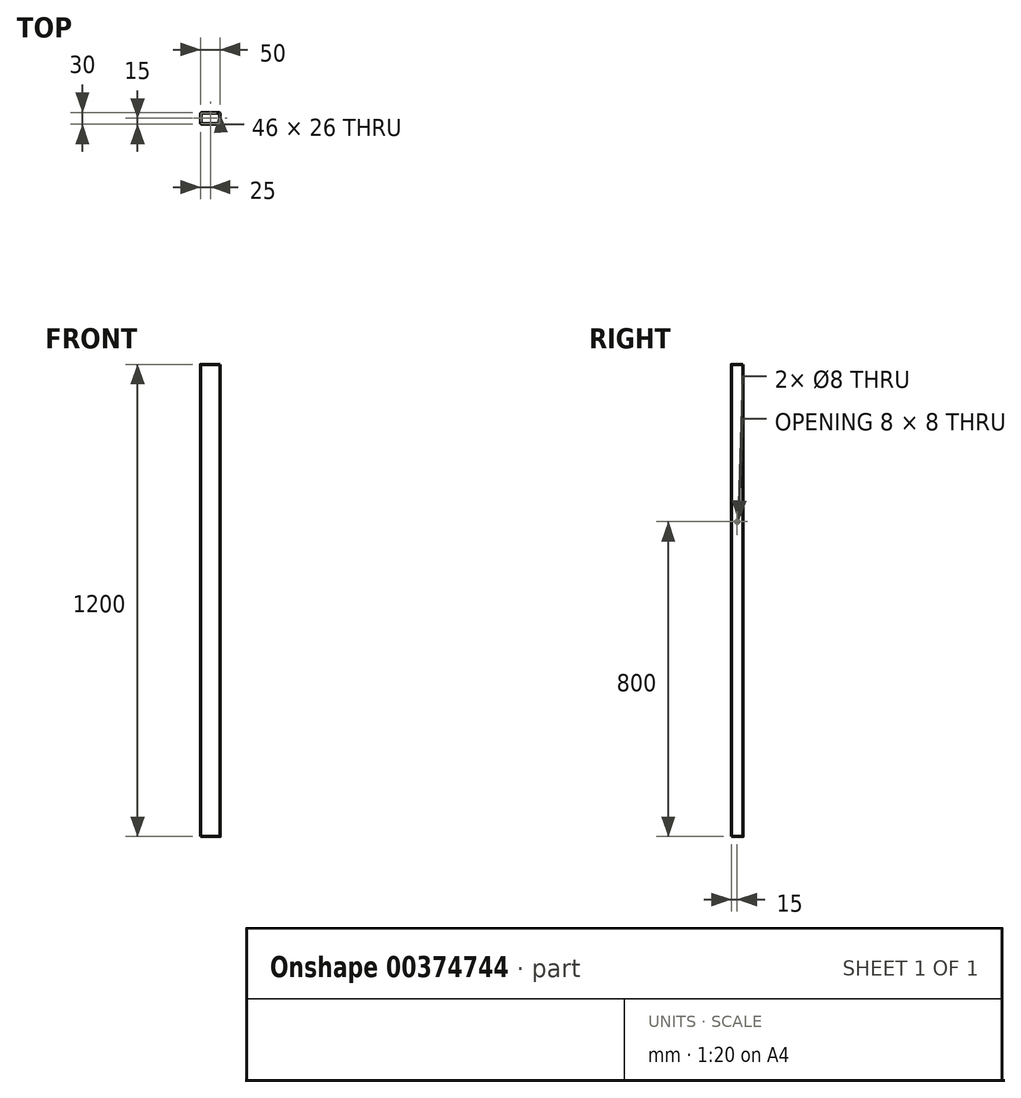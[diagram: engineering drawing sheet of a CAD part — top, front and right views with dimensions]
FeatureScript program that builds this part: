
annotation { "Feature Type Name" : "Feature", "Feature Type Description" : "" }
export const myFeature = defineFeature(function(context is Context, id is Id, definition is map)
    precondition{}
    {
        {
            var Q0;
            Q0=qCreatedBy(makeId("Top.planeOp"),FACE);
            var sketch = newSketch(context, id + "F0", { "sketchPlane" : qUnion([Q0])});
            skLineSegment(sketch, "E0.bottom", {"start": v(21.5, 15) * mm, "end": v(-21.5, 15) * mm});
            skLineSegment(sketch, "E0.top", {"start": v(21.5, -15) * mm, "end": v(-21.5, -15) * mm});
            skLineSegment(sketch, "E0.left", {"start": v(25, 11.5) * mm, "end": v(25, -11.5) * mm});
            skLineSegment(sketch, "E0.right", {"start": v(-25, 11.5) * mm, "end": v(-25, -11.5) * mm});
            skPoint(sketch, "E0.middle", {"position": v(0, 0) * mm});
            skLineSegment(sketch, "E1.bottom", {"start": v(23, -13) * mm, "end": v(-23, -13) * mm});
            skLineSegment(sketch, "E1.top", {"start": v(23, 13) * mm, "end": v(-23, 13) * mm});
            skLineSegment(sketch, "E1.left", {"start": v(23, -13) * mm, "end": v(23, 13) * mm});
            skLineSegment(sketch, "E1.right", {"start": v(-23, -13) * mm, "end": v(-23, 13) * mm});
            skPoint(sketch, "E2.visualSharp", {"position": v(-25, 15) * mm});
            skArc(sketch, "E2.filletArc", {"start": v(-21.5, 15) * mm, "mid": v(-23.97, 13.97) * mm, "end": v(-25, 11.5) * mm});
            skPoint(sketch, "E3.visualSharp", {"position": v(-25, -15) * mm});
            skArc(sketch, "E3.filletArc", {"start": v(-25, -11.5) * mm, "mid": v(-23.97, -13.97) * mm, "end": v(-21.5, -15) * mm});
            skPoint(sketch, "E4.visualSharp", {"position": v(25, -15) * mm});
            skArc(sketch, "E4.filletArc", {"start": v(21.5, -15) * mm, "mid": v(23.97, -13.97) * mm, "end": v(25, -11.5) * mm});
            skPoint(sketch, "E5.visualSharp", {"position": v(25, 15) * mm});
            skArc(sketch, "E5.filletArc", {"start": v(25, 11.5) * mm, "mid": v(23.97, 13.97) * mm, "end": v(21.5, 15) * mm});
            skSolve(sketch);
        }
        {
            var Q0;
            Q0=makeQuery(id+"F0.imprint","IMPRINT",FACE,{"disambiguationData":[TD([[makeQuery(id+"F0.imprint","IMPRINT",EDGE,{"derivedFrom":sQuery(id+"F0.wireOp",EDGE,"E0.bottom")}),1.0]])]});
            extrude(context, id + "F1", {"entities" : qUnion([Q0]), "depth" : 1200 * mm});
        }
        {
            var Q0;
            Q0=makeQuery(id+"F1.opExtrude","SWEPT_FACE",FACE,{"disambiguationData":[OSD([sQuery(id+"F0.wireOp",EDGE,"E0.left")])]});
            var sketch = newSketch(context, id + "F2", { "sketchPlane" : qUnion([Q0])});
            skPoint(sketch, "E6", {"position": v(0, 800) * mm});
            skSolve(sketch);
        }
        {
            var Q0;
            Q0=sQuery(id+"F2.wireOp",VERTEX,"E6");
            var Q1;
            Q1=makeQuery(id+"F1.opExtrude","SWEPT_BODY",BODY,{"disambiguationData":[OSD([sQuery(id+"F0.wireOp",EDGE,"E0.bottom"),sQuery(id+"F0.wireOp",EDGE,"E0.top"),sQuery(id+"F0.wireOp",EDGE,"E0.left"),sQuery(id+"F0.wireOp",EDGE,"E0.right"),sQuery(id+"F0.wireOp",EDGE,"E1.bottom"),sQuery(id+"F0.wireOp",EDGE,"E1.top"),sQuery(id+"F0.wireOp",EDGE,"E1.left"),sQuery(id+"F0.wireOp",EDGE,"E1.right"),sQuery(id+"F0.wireOp",EDGE,"E2.filletArc"),sQuery(id+"F0.wireOp",EDGE,"E3.filletArc"),sQuery(id+"F0.wireOp",EDGE,"E4.filletArc"),sQuery(id+"F0.wireOp",EDGE,"E5.filletArc")])]});
            hole(context, id + "F3", {"style" : HoleStyle.SIMPLE, "endStyle" : HoleEndStyle.THROUGH, "holeDiameter" : 8 * mm, "isTappedThrough" : true, "tappedDepth" : 12 * mm, "tapClearance" : 3, "locations" : qUnion([Q0]), "scope" : qUnion([Q1])});
        }
    });
